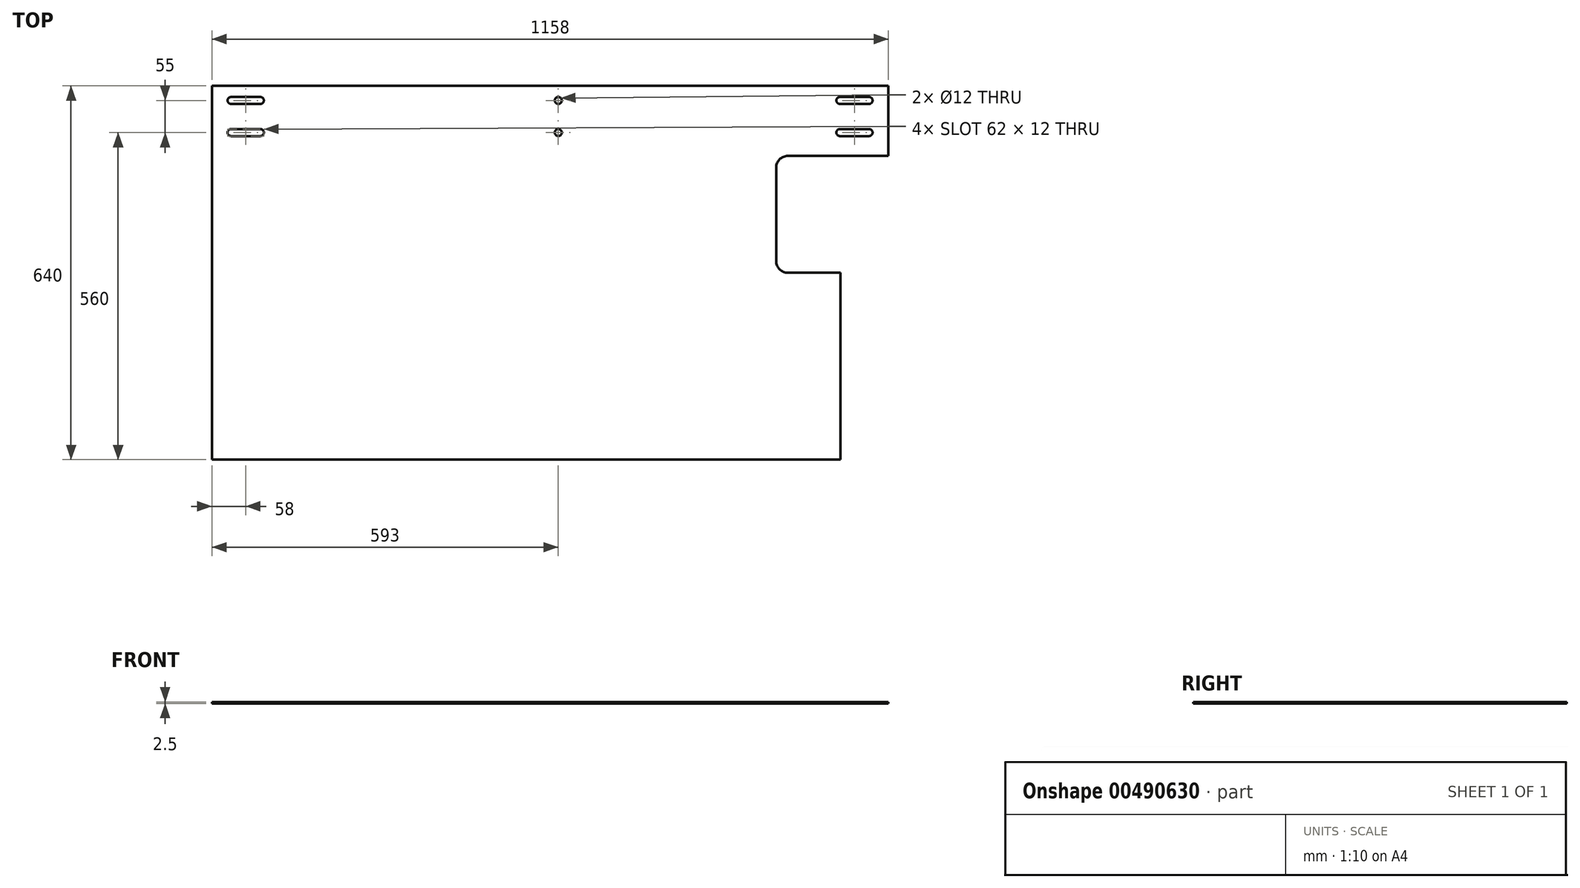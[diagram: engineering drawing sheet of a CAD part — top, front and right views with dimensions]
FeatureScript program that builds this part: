
annotation { "Feature Type Name" : "Feature", "Feature Type Description" : "" }
export const myFeature = defineFeature(function(context is Context, id is Id, definition is map)
    precondition{}
    {
        {
            var Q0;
            Q0=qCreatedBy(makeId("Top.planeOp"),FACE);
            var sketch = newSketch(context, id + "F0", { "sketchPlane" : qUnion([Q0])});
            skLineSegment(sketch, "E0", {"start": v(0, 0) * mm, "end": v(1076, 0) * mm});
            skLineSegment(sketch, "E1", {"start": v(1076, 0) * mm, "end": v(1076, 320) * mm});
            skLineSegment(sketch, "E2", {"start": v(1076, 320) * mm, "end": v(986, 320) * mm});
            skLineSegment(sketch, "E3", {"start": v(1158, 520) * mm, "end": v(1158, 640) * mm});
            skLineSegment(sketch, "E4", {"start": v(1158, 640) * mm, "end": v(0, 640) * mm});
            skLineSegment(sketch, "E5", {"start": v(0, 640) * mm, "end": v(0, 0) * mm});
            skLineSegment(sketch, "E6", {"start": v(33, 621) * mm, "end": v(83, 621) * mm});
            skLineSegment(sketch, "E7", {"start": v(33, 609) * mm, "end": v(83, 609) * mm});
            skArc(sketch, "E8", {"start": v(33, 621) * mm, "mid": v(27, 615) * mm, "end": v(33, 609) * mm});
            skArc(sketch, "E9", {"start": v(83, 621) * mm, "mid": v(89, 615) * mm, "end": v(83, 609) * mm});
            skLineSegment(sketch, "E10", {"start": v(58, 621) * mm, "end": v(58, 609) * mm, "construction": true});
            skLineSegment(sketch, "E11.0.1.0", {"start": v(33, 566) * mm, "end": v(83, 566) * mm});
            skArc(sketch, "E11.0.1.1", {"start": v(33, 566) * mm, "mid": v(27, 560) * mm, "end": v(33, 554) * mm});
            skLineSegment(sketch, "E11.0.1.2", {"start": v(33, 554) * mm, "end": v(83, 554) * mm});
            skArc(sketch, "E11.0.1.3", {"start": v(83, 566) * mm, "mid": v(89, 560) * mm, "end": v(83, 554) * mm});
            skLineSegment(sketch, "E11.1.0.0", {"start": v(1075, 621) * mm, "end": v(1125, 621) * mm});
            skArc(sketch, "E11.1.0.1", {"start": v(1075, 621) * mm, "mid": v(1069, 615) * mm, "end": v(1075, 609) * mm});
            skLineSegment(sketch, "E11.1.0.2", {"start": v(1075, 609) * mm, "end": v(1125, 609) * mm});
            skArc(sketch, "E11.1.0.3", {"start": v(1125, 621) * mm, "mid": v(1131, 615) * mm, "end": v(1125, 609) * mm});
            skLineSegment(sketch, "E11.1.1.0", {"start": v(1075, 566) * mm, "end": v(1125, 566) * mm});
            skArc(sketch, "E11.1.1.1", {"start": v(1075, 566) * mm, "mid": v(1069, 560) * mm, "end": v(1075, 554) * mm});
            skLineSegment(sketch, "E11.1.1.2", {"start": v(1075, 554) * mm, "end": v(1125, 554) * mm});
            skArc(sketch, "E11.1.1.3", {"start": v(1125, 566) * mm, "mid": v(1131, 560) * mm, "end": v(1125, 554) * mm});
            skLineSegment(sketch, "E11.direction1", {"start": v(33, 609) * mm, "end": v(1075, 609) * mm, "construction": true});
            skLineSegment(sketch, "E11.direction2", {"start": v(33, 609) * mm, "end": v(33, 554) * mm, "construction": true});
            skLineSegment(sketch, "E12", {"start": v(1100, 621) * mm, "end": v(1100, 609) * mm, "construction": true});
            skCircle(sketch, "E13", {"center": v(593, 615) * mm, "radius": 6 * mm});
            skCircle(sketch, "E14", {"center": v(593, 560) * mm, "radius": 6 * mm});
            skLineSegment(sketch, "E15.trimOffspring", {"start": v(986, 520) * mm, "end": v(1158, 520) * mm});
            skLineSegment(sketch, "E16.trimOffspring", {"start": v(966, 340) * mm, "end": v(966, 500) * mm});
            skPoint(sketch, "E17.visualSharp", {"position": v(966, 520) * mm});
            skArc(sketch, "E17.filletArc", {"start": v(986, 520) * mm, "mid": v(971.86, 514.14) * mm, "end": v(966, 500) * mm});
            skPoint(sketch, "E18.visualSharp", {"position": v(966, 320) * mm});
            skArc(sketch, "E18.filletArc", {"start": v(966, 340) * mm, "mid": v(971.86, 325.86) * mm, "end": v(986, 320) * mm});
            skSolve(sketch);
        }
        {
            var Q0;
            Q0=makeQuery(id+"F0.imprint","IMPRINT",FACE,{"disambiguationData":[TD([[makeQuery(id+"F0.imprint","IMPRINT",EDGE,{"derivedFrom":sQuery(id+"F0.wireOp",EDGE,"E0")}),1.0]])]});
            extrude(context, id + "F1", {"entities" : qUnion([Q0]), "depth" : 2.5 * mm});
        }
    });
